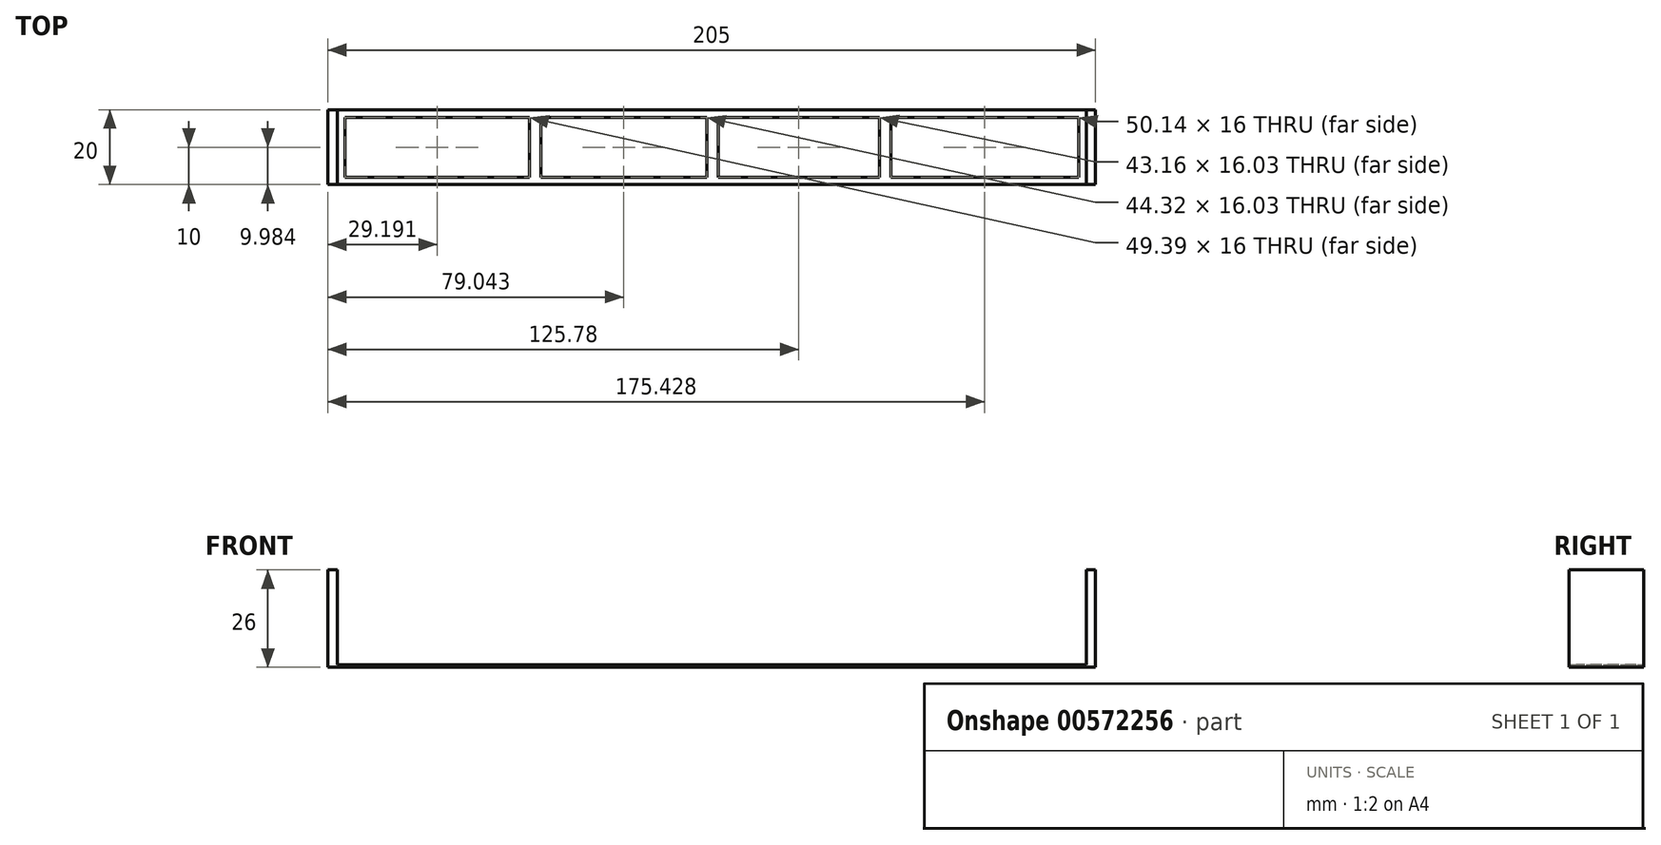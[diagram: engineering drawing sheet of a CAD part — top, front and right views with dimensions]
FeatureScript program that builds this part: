
annotation { "Feature Type Name" : "Feature", "Feature Type Description" : "" }
export const myFeature = defineFeature(function(context is Context, id is Id, definition is map)
    precondition{}
    {
        {
            var Q0;
            Q0=qCreatedBy(makeId("Top.planeOp"),FACE);
            var sketch = newSketch(context, id + "F0", { "sketchPlane" : qUnion([Q0])});
            skLineSegment(sketch, "E0", {"start": v(-52.32, 0) * mm, "end": v(147.68, 0) * mm});
            skLineSegment(sketch, "E1", {"start": v(147.68, 0) * mm, "end": v(147.68, -20) * mm});
            skLineSegment(sketch, "E2", {"start": v(147.68, -20) * mm, "end": v(-52.32, -20) * mm});
            skLineSegment(sketch, "E3", {"start": v(-52.32, -20) * mm, "end": v(-52.32, 0) * mm});
            skSolve(sketch);
        }
        {
            var Q0;
            Q0 = qSketchRegion(id + "F0", true);
            extrude(context, id + "F1", {"entities" : qUnion([Q0]), "depth" : 0.6 * mm, "offsetDistance" : 25 * mm});
        }
        {
            var Q0;
            Q0=makeQuery(id+"F1.opExtrude","CAP_FACE",FACE,{"disambiguationData":[OSD([sQuery(id+"F0.wireOp",EDGE,"E0"),sQuery(id+"F0.wireOp",EDGE,"E1"),sQuery(id+"F0.wireOp",EDGE,"E2"),sQuery(id+"F0.wireOp",EDGE,"E3")])],"isStart":false});
            var sketch = newSketch(context, id + "F2", { "sketchPlane" : qUnion([Q0])});
            skLineSegment(sketch, "E4.bottom", {"start": v(-50.32, -2) * mm, "end": v(-0.94, -2) * mm});
            skLineSegment(sketch, "E4.top", {"start": v(-50.32, -18) * mm, "end": v(-0.94, -18) * mm});
            skLineSegment(sketch, "E4.left", {"start": v(-50.32, -2) * mm, "end": v(-50.32, -18) * mm});
            skLineSegment(sketch, "E4.right", {"start": v(-0.94, -2) * mm, "end": v(-0.94, -18) * mm});
            skLineSegment(sketch, "E5.bottom", {"start": v(95.54, -2) * mm, "end": v(145.68, -2) * mm});
            skLineSegment(sketch, "E5.top", {"start": v(95.54, -18) * mm, "end": v(145.68, -18) * mm});
            skLineSegment(sketch, "E5.left", {"start": v(95.54, -2) * mm, "end": v(95.54, -18) * mm});
            skLineSegment(sketch, "E5.right", {"start": v(145.68, -2) * mm, "end": v(145.68, -18) * mm});
            skLineSegment(sketch, "E6.bottom", {"start": v(2.06, -2) * mm, "end": v(46.38, -2) * mm});
            skLineSegment(sketch, "E6.top", {"start": v(2.06, -18.03) * mm, "end": v(46.38, -18.03) * mm});
            skLineSegment(sketch, "E6.left", {"start": v(2.06, -2) * mm, "end": v(2.06, -18.03) * mm});
            skLineSegment(sketch, "E6.right", {"start": v(46.38, -2) * mm, "end": v(46.38, -18.03) * mm});
            skLineSegment(sketch, "E7.bottom", {"start": v(49.38, -2) * mm, "end": v(92.54, -2) * mm});
            skLineSegment(sketch, "E7.top", {"start": v(49.38, -18.03) * mm, "end": v(92.54, -18.03) * mm});
            skLineSegment(sketch, "E7.left", {"start": v(49.38, -2) * mm, "end": v(49.38, -18.03) * mm});
            skLineSegment(sketch, "E7.right", {"start": v(92.54, -2) * mm, "end": v(92.54, -18.03) * mm});
            skSolve(sketch);
        }
        {
            var Q0;
            Q0=qCreatedBy(makeId("Top.planeOp"),FACE);
            var sketch = newSketch(context, id + "F3", { "sketchPlane" : qUnion([Q0])});
            skLineSegment(sketch, "E8.bottom", {"start": v(-52.32, 0) * mm, "end": v(-54.82, 0) * mm});
            skLineSegment(sketch, "E8.top", {"start": v(-52.32, -20) * mm, "end": v(-54.82, -20) * mm});
            skLineSegment(sketch, "E8.left", {"start": v(-52.32, 0) * mm, "end": v(-52.32, -20) * mm});
            skLineSegment(sketch, "E8.right", {"start": v(-54.82, 0) * mm, "end": v(-54.82, -20) * mm});
            skLineSegment(sketch, "E9.bottom", {"start": v(150.18, 0) * mm, "end": v(147.68, 0) * mm});
            skLineSegment(sketch, "E9.top", {"start": v(150.18, -20) * mm, "end": v(147.68, -20) * mm});
            skLineSegment(sketch, "E9.left", {"start": v(150.18, 0) * mm, "end": v(150.18, -20) * mm});
            skLineSegment(sketch, "E9.right", {"start": v(147.68, 0) * mm, "end": v(147.68, -20) * mm});
            skSolve(sketch);
        }
        {
            var Q0;
            Q0=makeQuery(id+"F3.imprint","IMPRINT",FACE,{"disambiguationData":[TD([[makeQuery(id+"F3.imprint","IMPRINT",EDGE,{"derivedFrom":sQuery(id+"F3.wireOp",EDGE,"E8.bottom")}),1.0]])]});
            var Q1;
            Q1=makeQuery(id+"F3.imprint","IMPRINT",FACE,{"disambiguationData":[TD([[makeQuery(id+"F3.imprint","IMPRINT",EDGE,{"derivedFrom":sQuery(id+"F3.wireOp",EDGE,"E9.bottom")}),1.0]])]});
            extrude(context, id + "F4", {"entities" : qUnion([Q0, Q1]), "operationType" : NewBodyOperationType.ADD, "depth" : 26 * mm, "offsetDistance" : 25 * mm});
        }
        {
            var Q0;
            Q0=makeQuery(id+"F2.imprint","IMPRINT",FACE,{"disambiguationData":[TD([[makeQuery(id+"F2.imprint","IMPRINT",EDGE,{"derivedFrom":sQuery(id+"F2.wireOp",EDGE,"E4.bottom")}),-1.0]])]});
            var Q1;
            Q1=makeQuery(id+"F2.imprint","IMPRINT",FACE,{"disambiguationData":[TD([[makeQuery(id+"F2.imprint","IMPRINT",EDGE,{"derivedFrom":sQuery(id+"F2.wireOp",EDGE,"E6.bottom")}),-1.0]])]});
            var Q2;
            Q2=makeQuery(id+"F2.imprint","IMPRINT",FACE,{"disambiguationData":[TD([[makeQuery(id+"F2.imprint","IMPRINT",EDGE,{"derivedFrom":sQuery(id+"F2.wireOp",EDGE,"E7.bottom")}),-1.0]])]});
            var Q3;
            Q3=makeQuery(id+"F2.imprint","IMPRINT",FACE,{"disambiguationData":[TD([[makeQuery(id+"F2.imprint","IMPRINT",EDGE,{"derivedFrom":sQuery(id+"F2.wireOp",EDGE,"E5.bottom")}),-1.0]])]});
            extrude(context, id + "F5", {"entities" : qUnion([Q0, Q1, Q2, Q3]), "operationType" : NewBodyOperationType.REMOVE, "oppositeDirection" : true, "depth" : 25 * mm, "offsetDistance" : 25 * mm});
        }
    });
